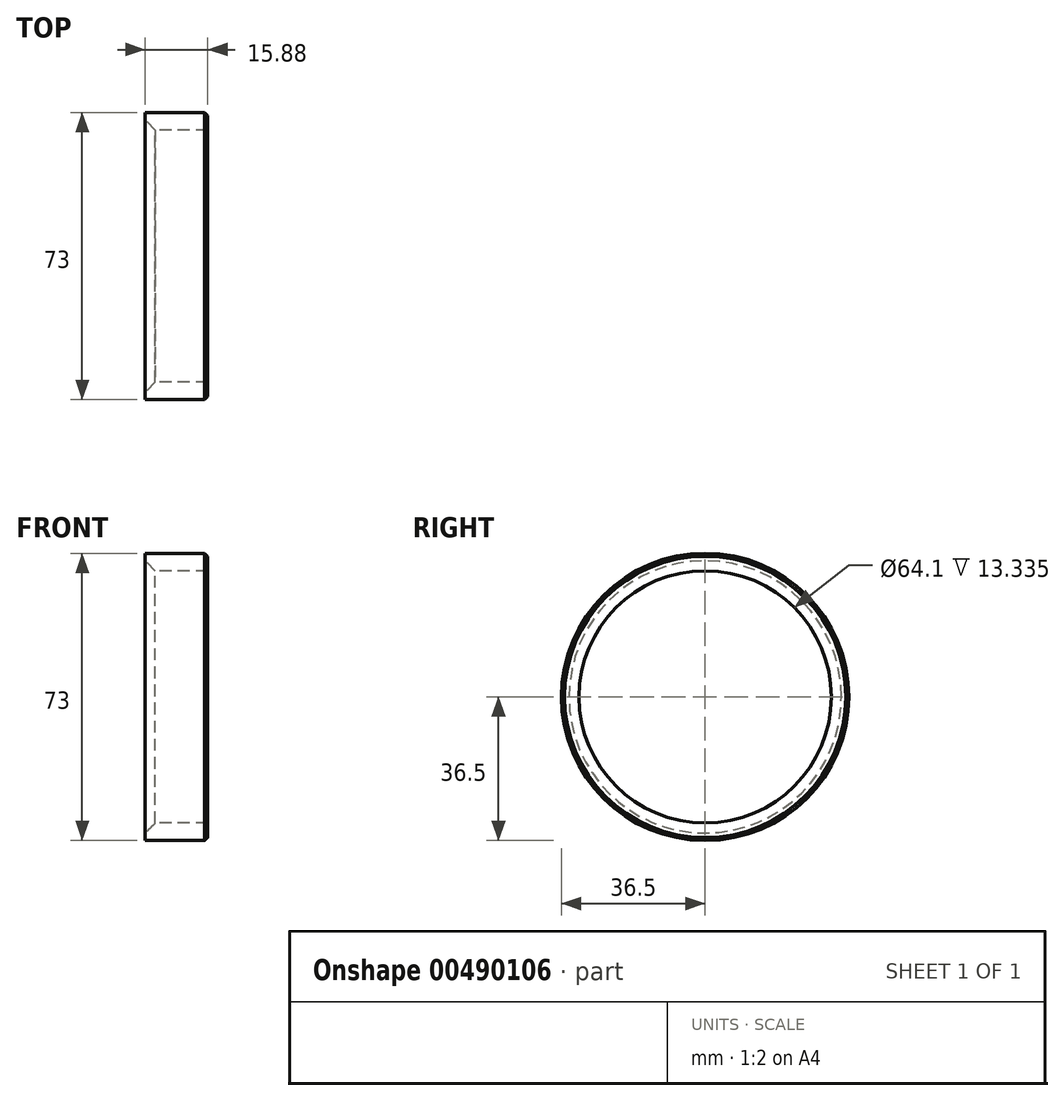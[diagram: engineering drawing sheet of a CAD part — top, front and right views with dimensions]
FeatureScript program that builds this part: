
annotation { "Feature Type Name" : "Feature", "Feature Type Description" : "" }
export const myFeature = defineFeature(function(context is Context, id is Id, definition is map)
    precondition{}
    {
        {
            var Q0;
            Q0=qCreatedBy(makeId("Right.planeOp"),FACE);
            var sketch = newSketch(context, id + "F0", { "sketchPlane" : qUnion([Q0])});
            skCircle(sketch, "E0", {"center": v(0, 0) * mm, "radius": 32.05 * mm});
            skCircle(sketch, "E1", {"center": v(0, 0) * mm, "radius": 36.5 * mm});
            skSolve(sketch);
        }
        {
            var Q0;
            Q0 = qSketchRegion(id + "F0", true);
            extrude(context, id + "F1", {"entities" : qUnion([Q0]), "depth" : 15.88 * mm});
        }
        {
            var Q0;
            Q0=makeQuery(id+"F1.opExtrude","CAP_EDGE",EDGE,{"disambiguationData":[OSD([sQuery(id+"F0.wireOp",EDGE,"E1")])],"isStart":false});
            chamfer(context, id + "F2", {"entities" : qUnion([Q0]), "width" : 0.76 * mm, "tangentPropagation" : true});
        }
        {
            var Q0;
            Q0=makeQuery(id+"F1.opExtrude","CAP_EDGE",EDGE,{"disambiguationData":[OSD([sQuery(id+"F0.wireOp",EDGE,"E0")])],"isStart":true});
            chamfer(context, id + "F3", {"entities" : qUnion([Q0]), "width" : 2.54 * mm, "tangentPropagation" : true});
        }
    });
